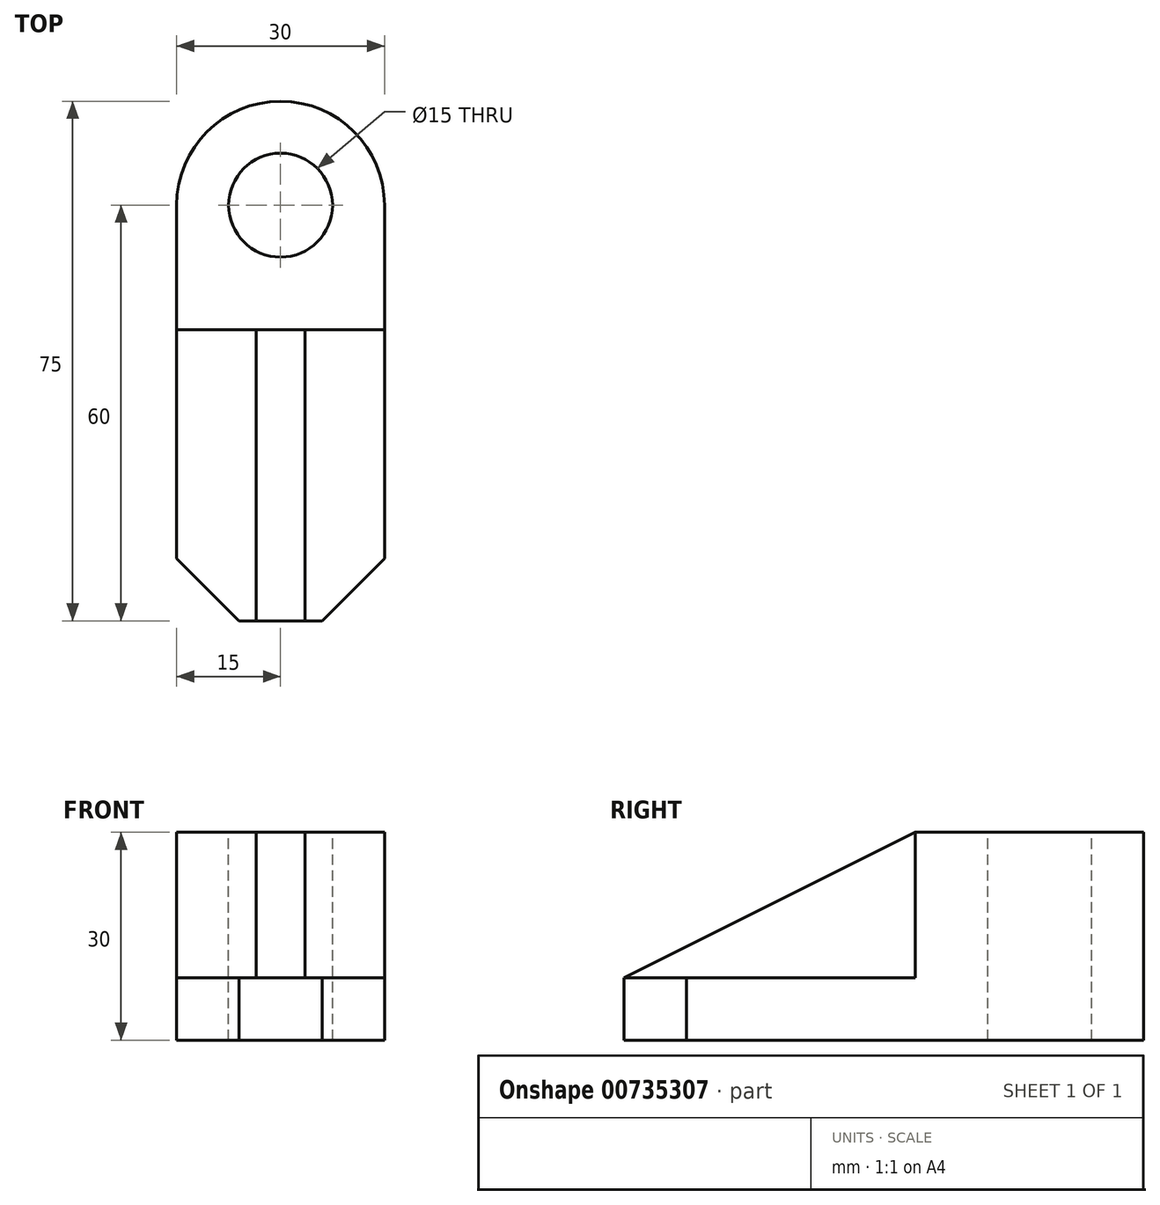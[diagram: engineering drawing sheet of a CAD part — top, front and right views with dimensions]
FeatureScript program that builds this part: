
annotation { "Feature Type Name" : "Feature", "Feature Type Description" : "" }
export const myFeature = defineFeature(function(context is Context, id is Id, definition is map)
    precondition{}
    {
        {
            var Q0;
            Q0=qCreatedBy(makeId("Top.planeOp"),FACE);
            var sketch = newSketch(context, id + "F0", { "sketchPlane" : qUnion([Q0])});
            skLineSegment(sketch, "E0.bottom", {"start": v(-15, 30) * mm, "end": v(15, 30) * mm});
            skLineSegment(sketch, "E0.top", {"start": v(-6, -30) * mm, "end": v(6, -30) * mm});
            skLineSegment(sketch, "E0.left", {"start": v(-15, 30) * mm, "end": v(-15, -21) * mm});
            skLineSegment(sketch, "E0.right", {"start": v(15, 30) * mm, "end": v(15, -21) * mm});
            skPoint(sketch, "E0.middle", {"position": v(0, 0) * mm});
            skLineSegment(sketch, "E1", {"start": v(-15, -21) * mm, "end": v(-6, -30) * mm});
            skPoint(sketch, "E2.orphan", {"position": v(-15, -30) * mm});
            skLineSegment(sketch, "E3", {"start": v(6, -30) * mm, "end": v(15, -21) * mm});
            skPoint(sketch, "E4.orphan", {"position": v(15, -30) * mm});
            skArc(sketch, "E5", {"start": v(15, 30) * mm, "mid": v(0, 45) * mm, "end": v(-15, 30) * mm});
            skSolve(sketch);
        }
        {
            var Q0;
            Q0=makeQuery(id+"F0.imprint","IMPRINT",FACE,{"disambiguationData":[TD([[makeQuery(id+"F0.imprint","IMPRINT",EDGE,{"derivedFrom":sQuery(id+"F0.wireOp",EDGE,"E0.bottom")}),-1.0]])]});
            extrude(context, id + "F1", {"entities" : qUnion([Q0]), "depth" : 9 * mm, "offsetDistance" : 25 * mm});
        }
        {
            var Q0;
            Q0=makeQuery(id+"F1.opExtrude","CAP_FACE",FACE,{"disambiguationData":[OSD([sQuery(id+"F0.wireOp",EDGE,"E0.bottom"),sQuery(id+"F0.wireOp",EDGE,"E0.top"),sQuery(id+"F0.wireOp",EDGE,"E0.left"),sQuery(id+"F0.wireOp",EDGE,"E0.right"),sQuery(id+"F0.wireOp",EDGE,"E1"),sQuery(id+"F0.wireOp",EDGE,"E3")])],"isStart":false});
            var sketch = newSketch(context, id + "F2", { "sketchPlane" : qUnion([Q0])});
            skLineSegment(sketch, "E6.bottom", {"start": v(-3.5, -30) * mm, "end": v(3.5, -30) * mm});
            skLineSegment(sketch, "E6.top", {"start": v(-3.5, 12) * mm, "end": v(3.5, 12) * mm});
            skLineSegment(sketch, "E6.left", {"start": v(-3.5, -30) * mm, "end": v(-3.5, 12) * mm});
            skLineSegment(sketch, "E6.right", {"start": v(3.5, -30) * mm, "end": v(3.5, 12) * mm});
            skSolve(sketch);
        }
        {
            var Q0;
            Q0=makeQuery(id+"F2.imprint","IMPRINT",FACE,{"disambiguationData":[TD([[makeQuery(id+"F2.imprint","IMPRINT",EDGE,{"derivedFrom":sQuery(id+"F2.wireOp",EDGE,"E6.bottom")}),1.0]])]});
            extrude(context, id + "F3", {"entities" : qUnion([Q0]), "operationType" : NewBodyOperationType.ADD, "depth" : 21 * mm, "offsetDistance" : 25 * mm});
        }
        {
            var Q0;
            Q0=makeQuery(id+"F3.opExtrude","SWEPT_FACE",FACE,{"disambiguationData":[OSD([sQuery(id+"F2.wireOp",EDGE,"E6.left")])]});
            var sketch = newSketch(context, id + "F4", { "sketchPlane" : qUnion([Q0])});
            skLineSegment(sketch, "E7", {"start": v(-12, 30) * mm, "end": v(30, 9) * mm});
            skSolve(sketch);
        }
        {
            var Q0;
            Q0=makeQuery(id+"F4.imprint","IMPRINT",FACE,{"disambiguationData":[TD([[makeQuery(id+"F4.imprint","IMPRINT",EDGE,{"derivedFrom":sQuery(id+"F4.wireOp",EDGE,"E7")}),1.0]])]});
            extrude(context, id + "F5", {"entities" : qUnion([Q0]), "operationType" : NewBodyOperationType.REMOVE, "oppositeDirection" : true, "depth" : 7 * mm, "offsetDistance" : 25 * mm});
        }
        {
            var Q0;
            Q0=makeQuery(id+"F1.opExtrude","CAP_FACE",FACE,{"disambiguationData":[OSD([sQuery(id+"F0.wireOp",EDGE,"E0.bottom"),sQuery(id+"F0.wireOp",EDGE,"E0.top"),sQuery(id+"F0.wireOp",EDGE,"E0.left"),sQuery(id+"F0.wireOp",EDGE,"E0.right"),sQuery(id+"F0.wireOp",EDGE,"E1"),sQuery(id+"F0.wireOp",EDGE,"E3")])],"isStart":false});
            var sketch = newSketch(context, id + "F6", { "sketchPlane" : qUnion([Q0])});
            skLineSegment(sketch, "E8", {"start": v(15, 12) * mm, "end": v(-15, 12) * mm});
            skSolve(sketch);
        }
        {
            var Q0;
            Q0=makeQuery(id+"F0.imprint","IMPRINT",FACE,{"disambiguationData":[TD([[makeQuery(id+"F0.imprint","IMPRINT",EDGE,{"derivedFrom":sQuery(id+"F0.wireOp",EDGE,"E0.bottom")}),1.0]])]});
            extrude(context, id + "F7", {"entities" : qUnion([Q0]), "operationType" : NewBodyOperationType.ADD, "depth" : 30 * mm, "offsetDistance" : 25 * mm});
        }
        {
            var Q0;
            {var subQ0=makeQuery(id+"F1.opExtrude","CAP_EDGE",EDGE,{"disambiguationData":[OSD([sQuery(id+"F0.wireOp",EDGE,"E0.bottom")])],"isStart":false});Q0=makeQuery(id+"F6.imprint","IMPRINT",FACE,{"disambiguationData":[TD([[makeQuery(id+"F6.imprint","IMPRINT",EDGE,{"derivedFrom":subQ0}),-1.0]])]});}
            extrude(context, id + "F8", {"entities" : qUnion([Q0]), "operationType" : NewBodyOperationType.ADD, "depth" : 21 * mm, "offsetDistance" : 25 * mm});
        }
        {
            var Q0;
            {var subQ0=sQuery(id+"F0.wireOp",EDGE,"E0.bottom");Q0=makeQuery(id+"F8.boolean.opBoolean","MERGE",FACE,{"derivedFrom":[makeQuery(id+"F7.opExtrude","CAP_FACE",FACE,{"disambiguationData":[OSD([subQ0,sQuery(id+"F0.wireOp",EDGE,"E5")])],"isStart":false}),makeQuery(id+"F8.opExtrude","CAP_FACE",FACE,{"disambiguationData":[OSD([subQ0,sQuery(id+"F0.wireOp",EDGE,"E0.left"),sQuery(id+"F0.wireOp",EDGE,"E0.right"),sQuery(id+"F6.wireOp",EDGE,"E8")])],"isStart":false})]});}
            var sketch = newSketch(context, id + "F9", { "sketchPlane" : qUnion([Q0])});
            skCircle(sketch, "E9", {"center": v(0, 30) * mm, "radius": 7.5 * mm});
            skSolve(sketch);
        }
        {
            var Q0;
            Q0=makeQuery(id+"F9.imprint","IMPRINT",FACE,{"disambiguationData":[TD([[makeQuery(id+"F9.imprint","IMPRINT",EDGE,{"derivedFrom":sQuery(id+"F9.wireOp",EDGE,"E9")}),1.0]])]});
            extrude(context, id + "F10", {"entities" : qUnion([Q0]), "operationType" : NewBodyOperationType.REMOVE, "oppositeDirection" : true, "depth" : 30 * mm, "offsetDistance" : 25 * mm});
        }
    });
